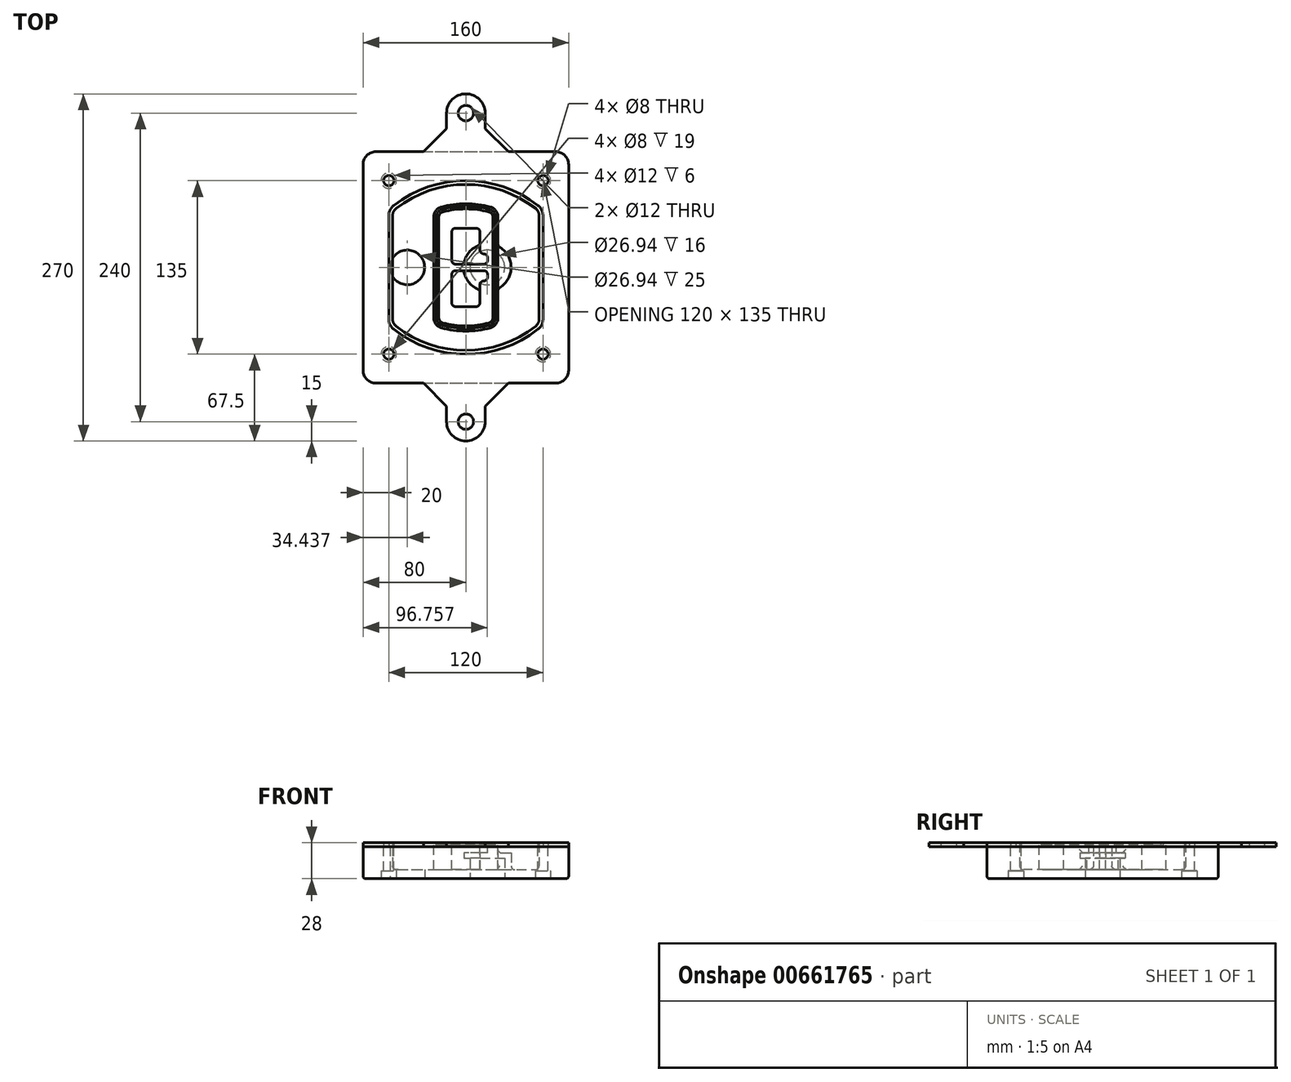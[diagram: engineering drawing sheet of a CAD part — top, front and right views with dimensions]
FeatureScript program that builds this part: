
annotation { "Feature Type Name" : "Feature", "Feature Type Description" : "" }
export const myFeature = defineFeature(function(context is Context, id is Id, definition is map)
    precondition{}
    {
        {
            var Q0;
            Q0=qCreatedBy(makeId("Top.planeOp"),FACE);
            var sketch = newSketch(context, id + "F0", { "sketchPlane" : qUnion([Q0])});
            skPoint(sketch, "E0.rect.middle", {"position": v(0, 0) * mm});
            skLineSegment(sketch, "E1.bottom", {"start": v(-70, -90) * mm, "end": v(70, -90) * mm});
            skLineSegment(sketch, "E1.top", {"start": v(-70, 90) * mm, "end": v(70, 90) * mm});
            skLineSegment(sketch, "E1.left", {"start": v(-80, -80) * mm, "end": v(-80, 80) * mm});
            skLineSegment(sketch, "E1.right", {"start": v(80, -80) * mm, "end": v(80, 80) * mm});
            skLineSegment(sketch, "E2", {"start": v(-80, 90) * mm, "end": v(80, -90) * mm, "construction": true});
            skLineSegment(sketch, "E3", {"start": v(80, 90) * mm, "end": v(-80, -90) * mm, "construction": true});
            skCircle(sketch, "E4", {"center": v(-60, 67.5) * mm, "radius": 4 * mm});
            skCircle(sketch, "E5", {"center": v(60, 67.5) * mm, "radius": 4 * mm});
            skCircle(sketch, "E6", {"center": v(60, -67.5) * mm, "radius": 4 * mm});
            skCircle(sketch, "E7", {"center": v(-60, -67.5) * mm, "radius": 4 * mm});
            skLineSegment(sketch, "E8", {"start": v(-60, 67.5) * mm, "end": v(60, 67.5) * mm, "construction": true});
            skLineSegment(sketch, "E9", {"start": v(60, 67.5) * mm, "end": v(60, -67.5) * mm, "construction": true});
            skLineSegment(sketch, "E10", {"start": v(60, -67.5) * mm, "end": v(-60, -67.5) * mm, "construction": true});
            skLineSegment(sketch, "E11", {"start": v(-60, -67.5) * mm, "end": v(-60, 67.5) * mm, "construction": true});
            skLineSegment(sketch, "E12", {"start": v(-60, 40.3) * mm, "end": v(-60, -40.3) * mm});
            skLineSegment(sketch, "E13", {"start": v(60, 40.3) * mm, "end": v(60, -40.3) * mm});
            skArc(sketch, "E14", {"start": v(56.15, 48.18) * mm, "mid": v(0, 67.5) * mm, "end": v(-56.15, 48.18) * mm});
            skArc(sketch, "E15", {"start": v(-56.15, -48.18) * mm, "mid": v(0, -67.5) * mm, "end": v(56.15, -48.18) * mm});
            skLineSegment(sketch, "E16", {"start": v(-60, 0) * mm, "end": v(60, 0) * mm, "construction": true});
            skPoint(sketch, "E17.visualSharp", {"position": v(-60, -45) * mm});
            skArc(sketch, "E17.filletArc", {"start": v(-60, -40.3) * mm, "mid": v(-58.99, -44.68) * mm, "end": v(-56.15, -48.18) * mm});
            skPoint(sketch, "E18.visualSharp", {"position": v(-60, 45) * mm});
            skArc(sketch, "E18.filletArc", {"start": v(-56.15, 48.18) * mm, "mid": v(-58.99, 44.68) * mm, "end": v(-60, 40.3) * mm});
            skPoint(sketch, "E19.visualSharp", {"position": v(60, 45) * mm});
            skArc(sketch, "E19.filletArc", {"start": v(60, 40.3) * mm, "mid": v(58.99, 44.68) * mm, "end": v(56.15, 48.18) * mm});
            skPoint(sketch, "E20.visualSharp", {"position": v(60, -45) * mm});
            skArc(sketch, "E20.filletArc", {"start": v(56.15, -48.18) * mm, "mid": v(58.99, -44.68) * mm, "end": v(60, -40.3) * mm});
            skPoint(sketch, "E21.visualSharp", {"position": v(-80, 90) * mm});
            skArc(sketch, "E21.filletArc", {"start": v(-70, 90) * mm, "mid": v(-77.07, 87.07) * mm, "end": v(-80, 80) * mm});
            skPoint(sketch, "E22.visualSharp", {"position": v(80, 90) * mm});
            skArc(sketch, "E22.filletArc", {"start": v(80, 80) * mm, "mid": v(77.07, 87.07) * mm, "end": v(70, 90) * mm});
            skPoint(sketch, "E23.visualSharp", {"position": v(80, -90) * mm});
            skArc(sketch, "E23.filletArc", {"start": v(70, -90) * mm, "mid": v(77.07, -87.07) * mm, "end": v(80, -80) * mm});
            skPoint(sketch, "E24.visualSharp", {"position": v(-80, -90) * mm});
            skArc(sketch, "E24.filletArc", {"start": v(-80, -80) * mm, "mid": v(-77.07, -87.07) * mm, "end": v(-70, -90) * mm});
            skArc(sketch, "E25.0", {"start": v(57, 40.3) * mm, "mid": v(56.3, 43.36) * mm, "end": v(54.3, 45.81) * mm});
            skLineSegment(sketch, "E25.1", {"start": v(57, 40.3) * mm, "end": v(57, -40.3) * mm});
            skArc(sketch, "E25.2", {"start": v(54.3, -45.81) * mm, "mid": v(56.3, -43.36) * mm, "end": v(57, -40.3) * mm});
            skArc(sketch, "E25.3", {"start": v(-54.3, -45.81) * mm, "mid": v(0, -64.5) * mm, "end": v(54.3, -45.81) * mm});
            skArc(sketch, "E25.4", {"start": v(-57, -40.3) * mm, "mid": v(-56.3, -43.36) * mm, "end": v(-54.3, -45.81) * mm});
            skArc(sketch, "E25.5", {"start": v(54.3, 45.81) * mm, "mid": v(0, 64.5) * mm, "end": v(-54.3, 45.81) * mm});
            skLineSegment(sketch, "E25.6", {"start": v(-57, 40.3) * mm, "end": v(-57, -40.3) * mm});
            skArc(sketch, "E25.7", {"start": v(-54.3, 45.81) * mm, "mid": v(-56.3, 43.36) * mm, "end": v(-57, 40.3) * mm});
            skArc(sketch, "E26.0", {"start": v(-58.62, 51.33) * mm, "mid": v(-62.58, 46.43) * mm, "end": v(-64, 40.3) * mm});
            skArc(sketch, "E26.1", {"start": v(58.62, 51.33) * mm, "mid": v(0, 71.5) * mm, "end": v(-58.62, 51.33) * mm});
            skArc(sketch, "E26.2", {"start": v(64, 40.3) * mm, "mid": v(62.58, 46.43) * mm, "end": v(58.62, 51.33) * mm});
            skLineSegment(sketch, "E26.3", {"start": v(64, 40.3) * mm, "end": v(64, -40.3) * mm});
            skArc(sketch, "E26.4", {"start": v(58.62, -51.33) * mm, "mid": v(62.58, -46.43) * mm, "end": v(64, -40.3) * mm});
            skLineSegment(sketch, "E26.5", {"start": v(-64, 40.3) * mm, "end": v(-64, -40.3) * mm});
            skArc(sketch, "E26.6", {"start": v(-58.62, -51.33) * mm, "mid": v(0, -71.5) * mm, "end": v(58.62, -51.33) * mm});
            skArc(sketch, "E26.7", {"start": v(-64, -40.3) * mm, "mid": v(-62.58, -46.43) * mm, "end": v(-58.62, -51.33) * mm});
            skSolve(sketch);
        }
        {
            var Q0;
            Q0=makeQuery(id+"F0.imprint","IMPRINT",FACE,{"disambiguationData":[TD([[makeQuery(id+"F0.imprint","IMPRINT",EDGE,{"derivedFrom":sQuery(id+"F0.wireOp",EDGE,"E1.bottom")}),1.0]])]});
            var Q1;
            Q1=makeQuery(id+"F0.imprint","IMPRINT",FACE,{"disambiguationData":[TD([[makeQuery(id+"F0.imprint","IMPRINT",EDGE,{"derivedFrom":sQuery(id+"F0.wireOp",EDGE,"E12")}),1.0]])]});
            var Q2;
            Q2=makeQuery(id+"F0.imprint","IMPRINT",FACE,{"disambiguationData":[TD([[makeQuery(id+"F0.imprint","IMPRINT",EDGE,{"derivedFrom":sQuery(id+"F0.wireOp",EDGE,"E25.0")}),1.0]])]});
            var Q3;
            Q3=makeQuery(id+"F0.imprint","IMPRINT",FACE,{"disambiguationData":[TD([[makeQuery(id+"F0.imprint","IMPRINT",EDGE,{"derivedFrom":sQuery(id+"F0.wireOp",EDGE,"E12")}),-1.0]])]});
            extrude(context, id + "F1", {"entities" : qUnion([Q0, Q1, Q2, Q3]), "oppositeDirection" : true, "depth" : 25 * mm});
        }
        {
            var Q0;
            Q0=makeQuery(id+"F0.imprint","IMPRINT",FACE,{"disambiguationData":[TD([[makeQuery(id+"F0.imprint","IMPRINT",EDGE,{"derivedFrom":sQuery(id+"F0.wireOp",EDGE,"E12")}),1.0]])]});
            extrude(context, id + "F2", {"entities" : qUnion([Q0]), "operationType" : NewBodyOperationType.ADD, "depth" : 3 * mm});
        }
        {
            var Q0;
            Q0=makeQuery(id+"F0.imprint","IMPRINT",FACE,{"disambiguationData":[TD([[makeQuery(id+"F0.imprint","IMPRINT",EDGE,{"derivedFrom":sQuery(id+"F0.wireOp",EDGE,"E25.0")}),1.0]])]});
            extrude(context, id + "F3", {"entities" : qUnion([Q0]), "operationType" : NewBodyOperationType.REMOVE, "oppositeDirection" : true, "depth" : 18 * mm});
        }
        {
            var Q0;
            Q0=makeQuery(id+"F2.opExtrude","CAP_FACE",FACE,{"disambiguationData":[OSD([sQuery(id+"F0.wireOp",EDGE,"E12"),sQuery(id+"F0.wireOp",EDGE,"E13"),sQuery(id+"F0.wireOp",EDGE,"E14"),sQuery(id+"F0.wireOp",EDGE,"E15"),sQuery(id+"F0.wireOp",EDGE,"E17.filletArc"),sQuery(id+"F0.wireOp",EDGE,"E18.filletArc"),sQuery(id+"F0.wireOp",EDGE,"E19.filletArc"),sQuery(id+"F0.wireOp",EDGE,"E20.filletArc"),sQuery(id+"F0.wireOp",EDGE,"E25.0"),sQuery(id+"F0.wireOp",EDGE,"E25.1"),sQuery(id+"F0.wireOp",EDGE,"E25.2"),sQuery(id+"F0.wireOp",EDGE,"E25.3"),sQuery(id+"F0.wireOp",EDGE,"E25.4"),sQuery(id+"F0.wireOp",EDGE,"E25.5"),sQuery(id+"F0.wireOp",EDGE,"E25.6"),sQuery(id+"F0.wireOp",EDGE,"E25.7")])],"isStart":false});
            var sketch = newSketch(context, id + "F4", { "sketchPlane" : qUnion([Q0])});
            skArc(sketch, "E27.0", {"start": v(-19.08, -46.97) * mm, "mid": v(0, -49.5) * mm, "end": v(19.08, -46.97) * mm});
            skArc(sketch, "E28.0", {"start": v(19.08, 46.97) * mm, "mid": v(0, 49.5) * mm, "end": v(-19.08, 46.97) * mm});
            skLineSegment(sketch, "E29", {"start": v(-25, 39.25) * mm, "end": v(-25, -39.25) * mm});
            skLineSegment(sketch, "E30", {"start": v(25, 39.25) * mm, "end": v(25, -39.25) * mm});
            skLineSegment(sketch, "E31", {"start": v(-25, 45.1) * mm, "end": v(25, 45.1) * mm, "construction": true});
            skLineSegment(sketch, "E32", {"start": v(-25, -45.1) * mm, "end": v(25, -45.1) * mm, "construction": true});
            skPoint(sketch, "E33.visualSharp", {"position": v(-25, 45.1) * mm});
            skArc(sketch, "E33.filletArc", {"start": v(-19.08, 46.97) * mm, "mid": v(-23.35, 44.11) * mm, "end": v(-25, 39.25) * mm});
            skPoint(sketch, "E34.visualSharp", {"position": v(25, 45.1) * mm});
            skArc(sketch, "E34.filletArc", {"start": v(25, 39.25) * mm, "mid": v(23.35, 44.11) * mm, "end": v(19.08, 46.97) * mm});
            skPoint(sketch, "E35.visualSharp", {"position": v(25, -45.1) * mm});
            skArc(sketch, "E35.filletArc", {"start": v(19.08, -46.97) * mm, "mid": v(23.35, -44.11) * mm, "end": v(25, -39.25) * mm});
            skPoint(sketch, "E36.visualSharp", {"position": v(-25, -45.1) * mm});
            skArc(sketch, "E36.filletArc", {"start": v(-25, -39.25) * mm, "mid": v(-23.35, -44.11) * mm, "end": v(-19.08, -46.97) * mm});
            skArc(sketch, "E37.0", {"start": v(54.3, 45.81) * mm, "mid": v(0, 64.5) * mm, "end": v(-54.3, 45.81) * mm});
            skArc(sketch, "E37.1", {"start": v(-54.3, 45.81) * mm, "mid": v(-56.3, 43.36) * mm, "end": v(-57, 40.3) * mm});
            skLineSegment(sketch, "E37.2", {"start": v(-57, 40.3) * mm, "end": v(-57, -40.3) * mm});
            skArc(sketch, "E37.3", {"start": v(-57, -40.3) * mm, "mid": v(-56.3, -43.36) * mm, "end": v(-54.3, -45.81) * mm});
            skArc(sketch, "E37.4", {"start": v(-54.3, -45.81) * mm, "mid": v(0, -64.5) * mm, "end": v(54.3, -45.81) * mm});
            skArc(sketch, "E37.5", {"start": v(54.3, -45.81) * mm, "mid": v(56.3, -43.36) * mm, "end": v(57, -40.3) * mm});
            skLineSegment(sketch, "E37.6", {"start": v(57, 40.3) * mm, "end": v(57, -40.3) * mm});
            skArc(sketch, "E37.7", {"start": v(57, 40.3) * mm, "mid": v(56.3, 43.36) * mm, "end": v(54.3, 45.81) * mm});
            skLineSegment(sketch, "E38.0", {"start": v(23, 39.25) * mm, "end": v(23, -39.25) * mm});
            skArc(sketch, "E38.1", {"start": v(18.56, -45.04) * mm, "mid": v(21.76, -42.9) * mm, "end": v(23, -39.25) * mm});
            skArc(sketch, "E38.2", {"start": v(-18.56, -45.04) * mm, "mid": v(0, -47.5) * mm, "end": v(18.56, -45.04) * mm});
            skArc(sketch, "E38.3", {"start": v(-23, -39.25) * mm, "mid": v(-21.76, -42.9) * mm, "end": v(-18.56, -45.04) * mm});
            skLineSegment(sketch, "E38.4", {"start": v(-23, 39.25) * mm, "end": v(-23, -39.25) * mm});
            skArc(sketch, "E38.5", {"start": v(23, 39.25) * mm, "mid": v(21.76, 42.9) * mm, "end": v(18.56, 45.04) * mm});
            skArc(sketch, "E38.6", {"start": v(-18.56, 45.04) * mm, "mid": v(-21.76, 42.9) * mm, "end": v(-23, 39.25) * mm});
            skArc(sketch, "E38.7", {"start": v(18.56, 45.04) * mm, "mid": v(0, 47.5) * mm, "end": v(-18.56, 45.04) * mm});
            skArc(sketch, "E39.0", {"start": v(21, 39.25) * mm, "mid": v(20.18, 41.68) * mm, "end": v(18.04, 43.1) * mm});
            skLineSegment(sketch, "E39.1", {"start": v(21, 39.25) * mm, "end": v(21, -39.25) * mm});
            skArc(sketch, "E39.2", {"start": v(18.04, -43.1) * mm, "mid": v(20.18, -41.68) * mm, "end": v(21, -39.25) * mm});
            skArc(sketch, "E39.3", {"start": v(-18.04, -43.1) * mm, "mid": v(0, -45.5) * mm, "end": v(18.04, -43.1) * mm});
            skArc(sketch, "E39.4", {"start": v(-21, -39.25) * mm, "mid": v(-20.18, -41.68) * mm, "end": v(-18.04, -43.1) * mm});
            skArc(sketch, "E39.5", {"start": v(18.04, 43.1) * mm, "mid": v(0, 45.5) * mm, "end": v(-18.04, 43.1) * mm});
            skLineSegment(sketch, "E39.6", {"start": v(-21, 39.25) * mm, "end": v(-21, -39.25) * mm});
            skArc(sketch, "E39.7", {"start": v(-18.04, 43.1) * mm, "mid": v(-20.18, 41.68) * mm, "end": v(-21, 39.25) * mm});
            skLineSegment(sketch, "E40", {"start": v(-25, 0) * mm, "end": v(25, 0) * mm, "construction": true});
            skLineSegment(sketch, "E41", {"start": v(-11, 5.5) * mm, "end": v(-11, 27.5) * mm});
            skLineSegment(sketch, "E42", {"start": v(-8, 30.5) * mm, "end": v(8, 30.5) * mm});
            skLineSegment(sketch, "E43", {"start": v(11, 27.5) * mm, "end": v(11, 13.5) * mm});
            skLineSegment(sketch, "E44", {"start": v(14, 10.5) * mm, "end": v(14, 10.5) * mm});
            skLineSegment(sketch, "E45", {"start": v(17, 7.5) * mm, "end": v(17, 5.5) * mm});
            skLineSegment(sketch, "E46", {"start": v(14, 2.5) * mm, "end": v(-8, 2.5) * mm});
            skPoint(sketch, "E47.visualSharp", {"position": v(-11, 30.5) * mm});
            skArc(sketch, "E47.filletArc", {"start": v(-8, 30.5) * mm, "mid": v(-10.12, 29.62) * mm, "end": v(-11, 27.5) * mm});
            skPoint(sketch, "E48.visualSharp", {"position": v(11, 30.5) * mm});
            skArc(sketch, "E48.filletArc", {"start": v(11, 27.5) * mm, "mid": v(10.12, 29.62) * mm, "end": v(8, 30.5) * mm});
            skPoint(sketch, "E49.visualSharp", {"position": v(11, 10.5) * mm});
            skArc(sketch, "E49.filletArc", {"start": v(11, 13.5) * mm, "mid": v(11.88, 11.38) * mm, "end": v(14, 10.5) * mm});
            skPoint(sketch, "E50.visualSharp", {"position": v(17, 10.5) * mm});
            skArc(sketch, "E50.filletArc", {"start": v(17, 7.5) * mm, "mid": v(16.12, 9.62) * mm, "end": v(14, 10.5) * mm});
            skPoint(sketch, "E51.visualSharp", {"position": v(17, 2.5) * mm});
            skArc(sketch, "E51.filletArc", {"start": v(14, 2.5) * mm, "mid": v(16.12, 3.38) * mm, "end": v(17, 5.5) * mm});
            skPoint(sketch, "E52.visualSharp", {"position": v(-11, 2.5) * mm});
            skArc(sketch, "E52.filletArc", {"start": v(-11, 5.5) * mm, "mid": v(-10.12, 3.38) * mm, "end": v(-8, 2.5) * mm});
            skLineSegment(sketch, "E53.0.MirrorCS", {"start": v(14, -2.5) * mm, "end": v(-8, -2.5) * mm});
            skArc(sketch, "E54.0.MirrorCS", {"start": v(-11, -5.5) * mm, "mid": v(-10.12, -3.38) * mm, "end": v(-8, -2.5) * mm});
            skLineSegment(sketch, "E55.0.MirrorCS", {"start": v(-11, -5.5) * mm, "end": v(-11, -27.5) * mm});
            skArc(sketch, "E56.0.MirrorCS", {"start": v(-8, -30.5) * mm, "mid": v(-10.12, -29.62) * mm, "end": v(-11, -27.5) * mm});
            skLineSegment(sketch, "E57.0.MirrorCS", {"start": v(-8, -30.5) * mm, "end": v(8, -30.5) * mm});
            skArc(sketch, "E58.0.MirrorCS", {"start": v(11, -27.5) * mm, "mid": v(10.12, -29.62) * mm, "end": v(8, -30.5) * mm});
            skLineSegment(sketch, "E59.0.MirrorCS", {"start": v(11, -27.5) * mm, "end": v(11, -13.5) * mm});
            skArc(sketch, "E60.0.MirrorCS", {"start": v(11, -13.5) * mm, "mid": v(11.88, -11.38) * mm, "end": v(14, -10.5) * mm});
            skArc(sketch, "E61.0.MirrorCS", {"start": v(17, -7.5) * mm, "mid": v(16.12, -9.62) * mm, "end": v(14, -10.5) * mm});
            skLineSegment(sketch, "E62.0.MirrorCS", {"start": v(17, -7.5) * mm, "end": v(17, -5.5) * mm});
            skArc(sketch, "E63.0.MirrorCS", {"start": v(14, -2.5) * mm, "mid": v(16.12, -3.38) * mm, "end": v(17, -5.5) * mm});
            skSolve(sketch);
        }
        {
            var Q0;
            Q0=makeQuery(id+"F4.imprint","IMPRINT",FACE,{"disambiguationData":[TD([[makeQuery(id+"F4.imprint","IMPRINT",EDGE,{"derivedFrom":sQuery(id+"F4.wireOp",EDGE,"E27.0")}),1.0]])]});
            var Q1;
            Q1=makeQuery(id+"F4.imprint","IMPRINT",FACE,{"disambiguationData":[TD([[makeQuery(id+"F4.imprint","IMPRINT",EDGE,{"derivedFrom":sQuery(id+"F4.wireOp",EDGE,"E38.0")}),-1.0]])]});
            var Q2;
            Q2=makeQuery(id+"F4.imprint","IMPRINT",FACE,{"disambiguationData":[TD([[makeQuery(id+"F4.imprint","IMPRINT",EDGE,{"derivedFrom":sQuery(id+"F4.wireOp",EDGE,"E39.0")}),1.0]])]});
            extrude(context, id + "F5", {"entities" : qUnion([Q0, Q1, Q2]), "operationType" : NewBodyOperationType.ADD, "endBound" : BoundingType.UP_TO_NEXT, "oppositeDirection" : true, "depth" : 25 * mm});
        }
        {
            var Q0;
            Q0=makeQuery(id+"F4.imprint","IMPRINT",FACE,{"disambiguationData":[TD([[makeQuery(id+"F4.imprint","IMPRINT",EDGE,{"derivedFrom":sQuery(id+"F4.wireOp",EDGE,"E38.0")}),-1.0]])]});
            extrude(context, id + "F6", {"entities" : qUnion([Q0]), "operationType" : NewBodyOperationType.REMOVE, "oppositeDirection" : true, "depth" : 2 * mm});
        }
        {
            var Q0;
            Q0=makeQuery(id+"F1.opExtrude","CAP_FACE",FACE,{"disambiguationData":[OSD([sQuery(id+"F0.wireOp",EDGE,"E1.bottom"),sQuery(id+"F0.wireOp",EDGE,"E1.top"),sQuery(id+"F0.wireOp",EDGE,"E1.left"),sQuery(id+"F0.wireOp",EDGE,"E1.right"),sQuery(id+"F0.wireOp",EDGE,"E4"),sQuery(id+"F0.wireOp",EDGE,"E5"),sQuery(id+"F0.wireOp",EDGE,"E6"),sQuery(id+"F0.wireOp",EDGE,"E7"),sQuery(id+"F0.wireOp",EDGE,"E21.filletArc"),sQuery(id+"F0.wireOp",EDGE,"E22.filletArc"),sQuery(id+"F0.wireOp",EDGE,"E23.filletArc"),sQuery(id+"F0.wireOp",EDGE,"E24.filletArc")])],"isStart":false});
            var sketch = newSketch(context, id + "F7", { "sketchPlane" : qUnion([Q0])});
            skCircle(sketch, "E64", {"center": v(16.76, 0) * mm, "radius": 13.47 * mm});
            skCircle(sketch, "E65", {"center": v(-45.56, 0) * mm, "radius": 13.47 * mm});
            skLineSegment(sketch, "E66", {"start": v(80, 0) * mm, "end": v(-80, 0) * mm});
            skCircle(sketch, "E67", {"center": v(16.76, 0) * mm, "radius": 18.47 * mm});
            skCircle(sketch, "E68", {"center": v(60, -67.5) * mm, "radius": 6 * mm});
            skCircle(sketch, "E69", {"center": v(-60, -67.5) * mm, "radius": 6 * mm});
            skCircle(sketch, "E70", {"center": v(-60, 67.5) * mm, "radius": 6 * mm});
            skCircle(sketch, "E71", {"center": v(60, 67.5) * mm, "radius": 6 * mm});
            skSolve(sketch);
        }
        {
            var Q0;
            {var subQ1=sQuery(id+"F7.wireOp",EDGE,"E66");var subQ4=sQuery(id+"F7.wireOp",EDGE,"E64");var subQ6=makeQuery(id+"F7.imprint","INTERSECT",VERTEX,{"disambiguationData":[OD(0.0)],"derivedFrom":[subQ4,subQ1]});Q0=makeQuery(id+"F7.imprint","IMPRINT",FACE,{"disambiguationData":[TD([[makeQuery(id+"F7.imprint","IMPRINT",EDGE,{"disambiguationData":[TD([[subQ6,-1.0]])],"derivedFrom":subQ4}),-1.0]])]});}
            var Q1;
            {var subQ0=sQuery(id+"F7.wireOp",EDGE,"E66");var subQ1=sQuery(id+"F7.wireOp",EDGE,"E64");var subQ3=makeQuery(id+"F7.imprint","INTERSECT",VERTEX,{"disambiguationData":[OD(0.0)],"derivedFrom":[subQ1,subQ0]});Q1=makeQuery(id+"F7.imprint","IMPRINT",FACE,{"disambiguationData":[TD([[makeQuery(id+"F7.imprint","IMPRINT",EDGE,{"disambiguationData":[TD([[subQ3,-1.0]])],"derivedFrom":subQ1}),1.0]])]});}
            var Q2;
            {var subQ0=sQuery(id+"F7.wireOp",EDGE,"E66");var subQ1=sQuery(id+"F7.wireOp",EDGE,"E64");var subQ3=makeQuery(id+"F7.imprint","INTERSECT",VERTEX,{"disambiguationData":[OD(0.0)],"derivedFrom":[subQ1,subQ0]});Q2=makeQuery(id+"F7.imprint","IMPRINT",FACE,{"disambiguationData":[TD([[makeQuery(id+"F7.imprint","IMPRINT",EDGE,{"disambiguationData":[TD([[subQ3,1.0]])],"derivedFrom":subQ1}),1.0]])]});}
            var Q3;
            {var subQ1=sQuery(id+"F7.wireOp",EDGE,"E66");var subQ4=sQuery(id+"F7.wireOp",EDGE,"E64");var subQ6=makeQuery(id+"F7.imprint","INTERSECT",VERTEX,{"disambiguationData":[OD(0.0)],"derivedFrom":[subQ4,subQ1]});Q3=makeQuery(id+"F7.imprint","IMPRINT",FACE,{"disambiguationData":[TD([[makeQuery(id+"F7.imprint","IMPRINT",EDGE,{"disambiguationData":[TD([[subQ6,1.0]])],"derivedFrom":subQ4}),-1.0]])]});}
            extrude(context, id + "F8", {"entities" : qUnion([Q0, Q1, Q2, Q3]), "operationType" : NewBodyOperationType.ADD, "oppositeDirection" : true, "depth" : 20 * mm});
        }
        {
            var Q0;
            {var subQ0=sQuery(id+"F7.wireOp",EDGE,"E66");var subQ1=sQuery(id+"F7.wireOp",EDGE,"E64");var subQ3=makeQuery(id+"F7.imprint","INTERSECT",VERTEX,{"disambiguationData":[OD(0.0)],"derivedFrom":[subQ1,subQ0]});Q0=makeQuery(id+"F7.imprint","IMPRINT",FACE,{"disambiguationData":[TD([[makeQuery(id+"F7.imprint","IMPRINT",EDGE,{"disambiguationData":[TD([[subQ3,-1.0]])],"derivedFrom":subQ1}),1.0]])]});}
            var Q1;
            {var subQ0=sQuery(id+"F7.wireOp",EDGE,"E66");var subQ1=sQuery(id+"F7.wireOp",EDGE,"E64");var subQ3=makeQuery(id+"F7.imprint","INTERSECT",VERTEX,{"disambiguationData":[OD(0.0)],"derivedFrom":[subQ1,subQ0]});Q1=makeQuery(id+"F7.imprint","IMPRINT",FACE,{"disambiguationData":[TD([[makeQuery(id+"F7.imprint","IMPRINT",EDGE,{"disambiguationData":[TD([[subQ3,1.0]])],"derivedFrom":subQ1}),1.0]])]});}
            extrude(context, id + "F9", {"entities" : qUnion([Q0, Q1]), "operationType" : NewBodyOperationType.REMOVE, "oppositeDirection" : true, "depth" : 16 * mm});
        }
        {
            var Q0;
            {var subQ0=sQuery(id+"F7.wireOp",EDGE,"E66");var subQ1=sQuery(id+"F7.wireOp",EDGE,"E65");var subQ3=makeQuery(id+"F7.imprint","INTERSECT",VERTEX,{"disambiguationData":[OD(0.0)],"derivedFrom":[subQ1,subQ0]});Q0=makeQuery(id+"F7.imprint","IMPRINT",FACE,{"disambiguationData":[TD([[makeQuery(id+"F7.imprint","IMPRINT",EDGE,{"disambiguationData":[TD([[subQ3,-1.0]])],"derivedFrom":subQ1}),1.0]])]});}
            var Q1;
            {var subQ0=sQuery(id+"F7.wireOp",EDGE,"E66");var subQ1=sQuery(id+"F7.wireOp",EDGE,"E65");var subQ3=makeQuery(id+"F7.imprint","INTERSECT",VERTEX,{"disambiguationData":[OD(0.0)],"derivedFrom":[subQ1,subQ0]});Q1=makeQuery(id+"F7.imprint","IMPRINT",FACE,{"disambiguationData":[TD([[makeQuery(id+"F7.imprint","IMPRINT",EDGE,{"disambiguationData":[TD([[subQ3,1.0]])],"derivedFrom":subQ1}),1.0]])]});}
            extrude(context, id + "F10", {"entities" : qUnion([Q0, Q1]), "operationType" : NewBodyOperationType.REMOVE, "oppositeDirection" : true, "depth" : 25 * mm});
        }
        {
            var Q0;
            Q0=makeQuery(id+"F7.imprint","IMPRINT",FACE,{"disambiguationData":[TD([[makeQuery(id+"F7.imprint","IMPRINT",EDGE,{"derivedFrom":sQuery(id+"F7.wireOp",EDGE,"E68")}),1.0]])]});
            var Q1;
            Q1=makeQuery(id+"F7.imprint","IMPRINT",FACE,{"disambiguationData":[TD([[makeQuery(id+"F7.imprint","IMPRINT",EDGE,{"derivedFrom":makeQuery(id+"F1.opExtrude","CAP_EDGE",EDGE,{"disambiguationData":[OSD([sQuery(id+"F0.wireOp",EDGE,"E5")])],"isStart":false})}),-1.0]])]});
            var Q2;
            Q2=makeQuery(id+"F7.imprint","IMPRINT",FACE,{"disambiguationData":[TD([[makeQuery(id+"F7.imprint","IMPRINT",EDGE,{"derivedFrom":sQuery(id+"F7.wireOp",EDGE,"E69")}),1.0]])]});
            var Q3;
            Q3=makeQuery(id+"F7.imprint","IMPRINT",FACE,{"disambiguationData":[TD([[makeQuery(id+"F7.imprint","IMPRINT",EDGE,{"derivedFrom":makeQuery(id+"F1.opExtrude","CAP_EDGE",EDGE,{"disambiguationData":[OSD([sQuery(id+"F0.wireOp",EDGE,"E4")])],"isStart":false})}),-1.0]])]});
            var Q4;
            Q4=makeQuery(id+"F7.imprint","IMPRINT",FACE,{"disambiguationData":[TD([[makeQuery(id+"F7.imprint","IMPRINT",EDGE,{"derivedFrom":sQuery(id+"F7.wireOp",EDGE,"E70")}),1.0]])]});
            var Q5;
            Q5=makeQuery(id+"F7.imprint","IMPRINT",FACE,{"disambiguationData":[TD([[makeQuery(id+"F7.imprint","IMPRINT",EDGE,{"derivedFrom":makeQuery(id+"F1.opExtrude","CAP_EDGE",EDGE,{"disambiguationData":[OSD([sQuery(id+"F0.wireOp",EDGE,"E7")])],"isStart":false})}),-1.0]])]});
            var Q6;
            Q6=makeQuery(id+"F7.imprint","IMPRINT",FACE,{"disambiguationData":[TD([[makeQuery(id+"F7.imprint","IMPRINT",EDGE,{"derivedFrom":sQuery(id+"F7.wireOp",EDGE,"E71")}),1.0]])]});
            var Q7;
            Q7=makeQuery(id+"F7.imprint","IMPRINT",FACE,{"disambiguationData":[TD([[makeQuery(id+"F7.imprint","IMPRINT",EDGE,{"derivedFrom":makeQuery(id+"F1.opExtrude","CAP_EDGE",EDGE,{"disambiguationData":[OSD([sQuery(id+"F0.wireOp",EDGE,"E6")])],"isStart":false})}),-1.0]])]});
            extrude(context, id + "F11", {"entities" : qUnion([Q0, Q1, Q2, Q3, Q4, Q5, Q6, Q7]), "operationType" : NewBodyOperationType.REMOVE, "oppositeDirection" : true, "depth" : 6 * mm});
        }
        {
            var Q0;
            Q0=makeQuery(id+"F9.boolean.opBoolean","COPY",FACE,{"derivedFrom":makeQuery(id+"F9.opExtrude","CAP_FACE",FACE,{"disambiguationData":[OSD([sQuery(id+"F7.wireOp",EDGE,"E64")])],"isStart":false})});
            var sketch = newSketch(context, id + "F12", { "sketchPlane" : qUnion([Q0])});
            skArc(sketch, "E72.0", {"start": v(11, 17.55) * mm, "mid": v(2.57, 11.82) * mm, "end": v(-1.54, 2.5) * mm});
            skArc(sketch, "E72.1", {"start": v(-1.54, -2.5) * mm, "mid": v(2.57, -11.82) * mm, "end": v(11, -17.55) * mm});
            skLineSegment(sketch, "E73", {"start": v(-1.54, -2.5) * mm, "end": v(14, -2.5) * mm});
            skLineSegment(sketch, "E74.0", {"start": v(14, 2.5) * mm, "end": v(-1.54, 2.5) * mm});
            skArc(sketch, "E74.1", {"start": v(14, 2.5) * mm, "mid": v(16.12, 3.38) * mm, "end": v(17, 5.5) * mm});
            skLineSegment(sketch, "E74.2", {"start": v(17, 7.5) * mm, "end": v(17, 5.5) * mm});
            skArc(sketch, "E74.3", {"start": v(17, 7.5) * mm, "mid": v(16.12, 9.62) * mm, "end": v(14, 10.5) * mm});
            skArc(sketch, "E74.4", {"start": v(11, 13.5) * mm, "mid": v(11.88, 11.38) * mm, "end": v(14, 10.5) * mm});
            skLineSegment(sketch, "E74.5", {"start": v(11, 17.55) * mm, "end": v(11, 13.5) * mm});
            skLineSegment(sketch, "E74.7", {"start": v(14, -2.5) * mm, "end": v(-1.54, -2.5) * mm});
            skArc(sketch, "E74.8", {"start": v(14, -2.5) * mm, "mid": v(16.12, -3.38) * mm, "end": v(17, -5.5) * mm});
            skLineSegment(sketch, "E74.9", {"start": v(17, -7.5) * mm, "end": v(17, -5.5) * mm});
            skArc(sketch, "E74.10", {"start": v(17, -7.5) * mm, "mid": v(16.12, -9.62) * mm, "end": v(14, -10.5) * mm});
            skArc(sketch, "E74.11", {"start": v(11, -13.5) * mm, "mid": v(11.88, -11.38) * mm, "end": v(14, -10.5) * mm});
            skLineSegment(sketch, "E74.12", {"start": v(11, -17.55) * mm, "end": v(11, -13.5) * mm});
            skPoint(sketch, "E75.orphan", {"position": v(11, -27.5) * mm});
            skPoint(sketch, "E76.orphan", {"position": v(-8, -2.5) * mm});
            skPoint(sketch, "E77.orphan", {"position": v(-8, 2.5) * mm});
            skPoint(sketch, "E78.orphan", {"position": v(11, 27.5) * mm});
            skSolve(sketch);
        }
        {
            var Q0;
            {var subQ7=sQuery(id+"F12.wireOp",EDGE,"E72.0");var subQ14=sQuery(id+"F12.wireOp",EDGE,"E72.1");var subQ16=sQuery(id+"F12.wireOp",EDGE,"E74.1");var subQ18=sQuery(id+"F12.wireOp",EDGE,"E74.8");Q0=qUnion([makeQuery(id+"F12.imprint","IMPRINT",FACE,{"disambiguationData":[TD([[makeQuery(id+"F12.imprint","IMPRINT",EDGE,{"derivedFrom":subQ7}),1.0]])]}),makeQuery(id+"F12.imprint","IMPRINT",FACE,{"disambiguationData":[TD([[makeQuery(id+"F12.imprint","IMPRINT",EDGE,{"derivedFrom":subQ14}),1.0]])]}),makeQuery(id+"F12.imprint","IMPRINT",FACE,{"disambiguationData":[TD([[makeQuery(id+"F12.imprint","IMPRINT",EDGE,{"derivedFrom":subQ16}),1.0]])]}),makeQuery(id+"F12.imprint","IMPRINT",FACE,{"disambiguationData":[TD([[makeQuery(id+"F12.imprint","IMPRINT",EDGE,{"derivedFrom":subQ18}),-1.0]])]})]);}
            var Q1;
            Q1=makeQuery(id+"F5.boolean.opBoolean","SPLIT",FACE,{"disambiguationData":[TD([makeQuery(id+"F5.opExtrude","SWEPT_FACE",FACE,{"disambiguationData":[OSD([sQuery(id+"F4.wireOp",EDGE,"E41")])]})])],"derivedFrom":makeQuery(id+"F3.boolean.opBoolean","COPY",FACE,{"derivedFrom":makeQuery(id+"F3.opExtrude","CAP_FACE",FACE,{"disambiguationData":[OSD([sQuery(id+"F0.wireOp",EDGE,"E25.0"),sQuery(id+"F0.wireOp",EDGE,"E25.1"),sQuery(id+"F0.wireOp",EDGE,"E25.2"),sQuery(id+"F0.wireOp",EDGE,"E25.3"),sQuery(id+"F0.wireOp",EDGE,"E25.4"),sQuery(id+"F0.wireOp",EDGE,"E25.5"),sQuery(id+"F0.wireOp",EDGE,"E25.6"),sQuery(id+"F0.wireOp",EDGE,"E25.7")])],"isStart":false})})});
            extrude(context, id + "F13", {"entities" : qUnion([Q0]), "operationType" : NewBodyOperationType.REMOVE, "endBound" : BoundingType.UP_TO_SURFACE, "endBoundEntityFace" : qUnion([Q1]), "depth" : 25 * mm});
        }
        {
            var Q0;
            Q0=makeQuery(id+"F3.boolean.opBoolean","COPY",EDGE,{"derivedFrom":makeQuery(id+"F3.opExtrude","CAP_EDGE",EDGE,{"disambiguationData":[OSD([sQuery(id+"F0.wireOp",EDGE,"E25.6")])],"isStart":false})});
            var Q1;
            Q1=makeQuery(id+"F8.boolean.opBoolean","INTERSECT",EDGE,{"derivedFrom":[makeQuery(id+"F5.opExtrude","SWEPT_FACE",FACE,{"disambiguationData":[OSD([sQuery(id+"F4.wireOp",EDGE,"E30")])]}),makeQuery(id+"F8.opExtrude","CAP_FACE",FACE,{"disambiguationData":[OSD([sQuery(id+"F7.wireOp",EDGE,"E67")])],"isStart":false})]});
            var Q2;
            Q2=makeQuery(id+"F8.boolean.opBoolean","INTERSECT",EDGE,{"disambiguationData":[OD(1.0)],"derivedFrom":[makeQuery(id+"F5.opExtrude","SWEPT_FACE",FACE,{"disambiguationData":[OSD([sQuery(id+"F4.wireOp",EDGE,"E30")])]}),makeQuery(id+"F8.opExtrude","SWEPT_FACE",FACE,{"disambiguationData":[OSD([sQuery(id+"F7.wireOp",EDGE,"E67")])]})]});
            var Q3;
            {var subQ0=makeQuery(id+"F3.boolean.opBoolean","COPY",FACE,{"derivedFrom":makeQuery(id+"F3.opExtrude","CAP_FACE",FACE,{"disambiguationData":[OSD([sQuery(id+"F0.wireOp",EDGE,"E25.0"),sQuery(id+"F0.wireOp",EDGE,"E25.1"),sQuery(id+"F0.wireOp",EDGE,"E25.2"),sQuery(id+"F0.wireOp",EDGE,"E25.3"),sQuery(id+"F0.wireOp",EDGE,"E25.4"),sQuery(id+"F0.wireOp",EDGE,"E25.5"),sQuery(id+"F0.wireOp",EDGE,"E25.6"),sQuery(id+"F0.wireOp",EDGE,"E25.7")])],"isStart":false})});var subQ1=sQuery(id+"F4.wireOp",EDGE,"E30");Q3=makeQuery(id+"F8.boolean.opBoolean","SPLIT",EDGE,{"disambiguationData":[TD([makeQuery(id+"F5.opExtrude","SWEPT_FACE",FACE,{"disambiguationData":[OSD([sQuery(id+"F4.wireOp",EDGE,"E35.filletArc")])]})])],"derivedFrom":makeQuery(id+"F5.opExtrude","TWEAK_EDGE",EDGE,{"derivedFrom":[subQ0,makeQuery(id+"F4.imprint","IMPRINT",EDGE,{"derivedFrom":subQ1})]})});}
            var Q4;
            {var subQ0=sQuery(id+"F0.wireOp",EDGE,"E25.0");var subQ1=sQuery(id+"F0.wireOp",EDGE,"E25.1");var subQ2=sQuery(id+"F0.wireOp",EDGE,"E25.2");var subQ3=sQuery(id+"F0.wireOp",EDGE,"E25.3");var subQ4=sQuery(id+"F0.wireOp",EDGE,"E25.4");var subQ5=sQuery(id+"F0.wireOp",EDGE,"E25.5");var subQ6=sQuery(id+"F0.wireOp",EDGE,"E25.6");var subQ7=sQuery(id+"F0.wireOp",EDGE,"E25.7");Q4=makeQuery(id+"F8.boolean.opBoolean","INTERSECT",EDGE,{"derivedFrom":[makeQuery(id+"F5.boolean.opBoolean","SPLIT",FACE,{"disambiguationData":[TD([makeQuery(id+"F2.opExtrude","SWEPT_FACE",FACE,{"disambiguationData":[OSD([subQ0])]})])],"derivedFrom":makeQuery(id+"F3.boolean.opBoolean","COPY",FACE,{"derivedFrom":makeQuery(id+"F3.opExtrude","CAP_FACE",FACE,{"disambiguationData":[OSD([subQ0,subQ1,subQ2,subQ3,subQ4,subQ5,subQ6,subQ7])],"isStart":false})})}),makeQuery(id+"F8.opExtrude","SWEPT_FACE",FACE,{"disambiguationData":[OSD([sQuery(id+"F7.wireOp",EDGE,"E67")])]})]});}
            var Q5;
            Q5=makeQuery(id+"F8.boolean.opBoolean","INTERSECT",EDGE,{"disambiguationData":[OD(0.0)],"derivedFrom":[makeQuery(id+"F5.opExtrude","SWEPT_FACE",FACE,{"disambiguationData":[OSD([sQuery(id+"F4.wireOp",EDGE,"E30")])]}),makeQuery(id+"F8.opExtrude","SWEPT_FACE",FACE,{"disambiguationData":[OSD([sQuery(id+"F7.wireOp",EDGE,"E67")])]})]});
            fillet(context, id + "F14", {"entities" : qUnion([Q0, Q1, Q2, Q3, Q4, Q5]), "radius" : 3 * mm, "tangentPropagation" : true, "allowEdgeOverflow" : false});
        }
        {
            var Q0;
            Q0=makeQuery(id+"F1.opExtrude","CAP_EDGE",EDGE,{"disambiguationData":[OSD([sQuery(id+"F0.wireOp",EDGE,"E1.bottom")])],"isStart":false});
            fillet(context, id + "F15", {"entities" : qUnion([Q0]), "radius" : 2 * mm, "tangentPropagation" : true, "allowEdgeOverflow" : false});
        }
        {
            var Q0;
            {var subQ0=sQuery(id+"F0.wireOp",EDGE,"E21.filletArc");var subQ1=sQuery(id+"F0.wireOp",EDGE,"E7");var subQ2=sQuery(id+"F0.wireOp",EDGE,"E6");var subQ3=sQuery(id+"F0.wireOp",EDGE,"E5");var subQ4=sQuery(id+"F0.wireOp",EDGE,"E4");var subQ5=sQuery(id+"F0.wireOp",EDGE,"E22.filletArc");var subQ6=sQuery(id+"F0.wireOp",EDGE,"E1.bottom");var subQ7=sQuery(id+"F0.wireOp",EDGE,"E1.right");var subQ8=sQuery(id+"F0.wireOp",EDGE,"E1.top");var subQ9=sQuery(id+"F0.wireOp",EDGE,"E1.left");var subQ10=sQuery(id+"F0.wireOp",EDGE,"E23.filletArc");var subQ11=sQuery(id+"F0.wireOp",EDGE,"E24.filletArc");Q0=makeQuery(id+"F2.boolean.opBoolean","SPLIT",FACE,{"disambiguationData":[TD([makeQuery(id+"F1.opExtrude","SWEPT_FACE",FACE,{"disambiguationData":[OSD([subQ6])]})])],"derivedFrom":makeQuery(id+"F1.opExtrude","CAP_FACE",FACE,{"disambiguationData":[OSD([subQ6,subQ8,subQ9,subQ7,subQ4,subQ3,subQ2,subQ1,subQ0,subQ5,subQ10,subQ11])],"isStart":true})});}
            var sketch = newSketch(context, id + "F16", { "sketchPlane" : qUnion([Q0])});
            skLineSegment(sketch, "E79.0", {"start": v(-70, 90) * mm, "end": v(70, 90) * mm});
            skArc(sketch, "E79.1", {"start": v(-70, 90) * mm, "mid": v(-77.07, 87.07) * mm, "end": v(-80, 80) * mm});
            skLineSegment(sketch, "E79.2", {"start": v(-80, -80) * mm, "end": v(-80, 80) * mm});
            skArc(sketch, "E79.3", {"start": v(-80, -80) * mm, "mid": v(-77.07, -87.07) * mm, "end": v(-70, -90) * mm});
            skLineSegment(sketch, "E79.4", {"start": v(-70, -90) * mm, "end": v(70, -90) * mm});
            skArc(sketch, "E79.5", {"start": v(70, -90) * mm, "mid": v(77.07, -87.07) * mm, "end": v(80, -80) * mm});
            skLineSegment(sketch, "E79.6", {"start": v(80, -80) * mm, "end": v(80, 80) * mm});
            skArc(sketch, "E79.7", {"start": v(80, 80) * mm, "mid": v(77.07, 87.07) * mm, "end": v(70, 90) * mm});
            skCircle(sketch, "E79.8", {"center": v(60, 67.5) * mm, "radius": 4 * mm});
            skCircle(sketch, "E79.9", {"center": v(-60, 67.5) * mm, "radius": 4 * mm});
            skCircle(sketch, "E79.10", {"center": v(-60, -67.5) * mm, "radius": 4 * mm});
            skCircle(sketch, "E79.11", {"center": v(60, -67.5) * mm, "radius": 4 * mm});
            skArc(sketch, "E79.12", {"start": v(56.15, 48.18) * mm, "mid": v(0, 67.5) * mm, "end": v(-56.15, 48.18) * mm});
            skArc(sketch, "E79.13", {"start": v(60, 40.3) * mm, "mid": v(58.99, 44.68) * mm, "end": v(56.15, 48.18) * mm});
            skLineSegment(sketch, "E79.14", {"start": v(60, 40.3) * mm, "end": v(60, -40.3) * mm});
            skArc(sketch, "E79.15", {"start": v(56.15, -48.18) * mm, "mid": v(58.99, -44.68) * mm, "end": v(60, -40.3) * mm});
            skArc(sketch, "E79.16", {"start": v(-56.15, -48.18) * mm, "mid": v(0, -67.5) * mm, "end": v(56.15, -48.18) * mm});
            skArc(sketch, "E79.17", {"start": v(-60, -40.3) * mm, "mid": v(-58.99, -44.68) * mm, "end": v(-56.15, -48.18) * mm});
            skLineSegment(sketch, "E79.18", {"start": v(-60, 40.3) * mm, "end": v(-60, -40.3) * mm});
            skArc(sketch, "E79.19", {"start": v(-56.15, 48.18) * mm, "mid": v(-58.99, 44.68) * mm, "end": v(-60, 40.3) * mm});
            skPoint(sketch, "E79.20", {"position": v(-77.07, -87.07) * mm});
            skLineSegment(sketch, "E80", {"start": v(0, 90) * mm, "end": v(0, 120) * mm, "construction": true});
            skPoint(sketch, "E80.endSnap0", {"position": v(0, 90) * mm});
            skCircle(sketch, "E81", {"center": v(0, 120) * mm, "radius": 6 * mm});
            skArc(sketch, "E82", {"start": v(15, 120) * mm, "mid": v(0, 135) * mm, "end": v(-15, 120) * mm});
            skLineSegment(sketch, "E83", {"start": v(15, 120) * mm, "end": v(15, 108) * mm});
            skLineSegment(sketch, "E84", {"start": v(33, 90) * mm, "end": v(15, 108) * mm});
            skLineSegment(sketch, "E85.MirrorCS", {"start": v(-15, 120) * mm, "end": v(-15, 108) * mm});
            skLineSegment(sketch, "E86.MirrorCS", {"start": v(-33, 90) * mm, "end": v(-15, 108) * mm});
            skLineSegment(sketch, "E87", {"start": v(-80, 0) * mm, "end": v(80, 0) * mm, "construction": true});
            skLineSegment(sketch, "E88.MirrorCS", {"start": v(-33, -90) * mm, "end": v(-15, -108) * mm});
            skLineSegment(sketch, "E89.MirrorCS", {"start": v(-15, -120) * mm, "end": v(-15, -108) * mm});
            skLineSegment(sketch, "E90.MirrorCS", {"start": v(0, -90) * mm, "end": v(0, -120) * mm, "construction": true});
            skCircle(sketch, "E91.MirrorC", {"center": v(0, -120) * mm, "radius": 6 * mm});
            skArc(sketch, "E92.MirrorCS", {"start": v(15, -120) * mm, "mid": v(0, -135) * mm, "end": v(-15, -120) * mm});
            skLineSegment(sketch, "E93.MirrorCS", {"start": v(15, -120) * mm, "end": v(15, -108) * mm});
            skLineSegment(sketch, "E94.MirrorCS", {"start": v(33, -90) * mm, "end": v(15, -108) * mm});
            skSolve(sketch);
        }
        {
            var Q0;
            Q0=qSketchRegion(id+"F16",true);
            var Q1;
            Q1=makeQuery(id+"F2.opExtrude","CAP_FACE",FACE,{"disambiguationData":[OSD([sQuery(id+"F0.wireOp",EDGE,"E12"),sQuery(id+"F0.wireOp",EDGE,"E13"),sQuery(id+"F0.wireOp",EDGE,"E14"),sQuery(id+"F0.wireOp",EDGE,"E15"),sQuery(id+"F0.wireOp",EDGE,"E17.filletArc"),sQuery(id+"F0.wireOp",EDGE,"E18.filletArc"),sQuery(id+"F0.wireOp",EDGE,"E19.filletArc"),sQuery(id+"F0.wireOp",EDGE,"E20.filletArc"),sQuery(id+"F0.wireOp",EDGE,"E25.0"),sQuery(id+"F0.wireOp",EDGE,"E25.1"),sQuery(id+"F0.wireOp",EDGE,"E25.2"),sQuery(id+"F0.wireOp",EDGE,"E25.3"),sQuery(id+"F0.wireOp",EDGE,"E25.4"),sQuery(id+"F0.wireOp",EDGE,"E25.5"),sQuery(id+"F0.wireOp",EDGE,"E25.6"),sQuery(id+"F0.wireOp",EDGE,"E25.7")])],"isStart":false});
            extrude(context, id + "F17", {"entities" : qUnion([Q0]), "endBound" : BoundingType.UP_TO_SURFACE, "endBoundEntityFace" : qUnion([Q1]), "depth" : 25 * mm});
        }
    });
